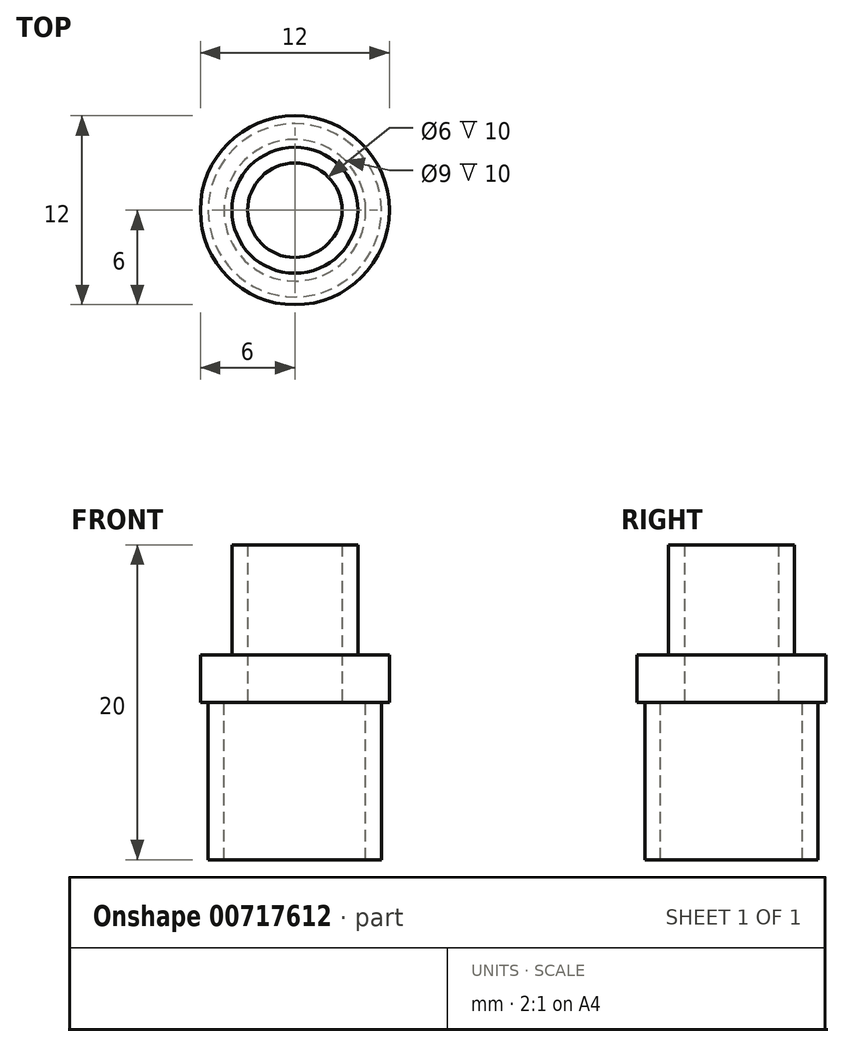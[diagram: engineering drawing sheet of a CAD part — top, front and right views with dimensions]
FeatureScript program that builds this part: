
annotation { "Feature Type Name" : "Feature", "Feature Type Description" : "" }
export const myFeature = defineFeature(function(context is Context, id is Id, definition is map)
    precondition{}
    {
        {
            var Q0;
            Q0=qCreatedBy(makeId("Top.planeOp"),FACE);
            var sketch = newSketch(context, id + "F0", { "sketchPlane" : qUnion([Q0])});
            skCircle(sketch, "E0", {"center": v(0, 0) * mm, "radius": 3 * mm});
            skCircle(sketch, "E1", {"center": v(0, 0) * mm, "radius": 4 * mm});
            skSolve(sketch);
        }
        {
            var Q0;
            Q0 = qSketchRegion(id + "F0", true);
            extrude(context, id + "F1", {"entities" : qUnion([Q0]), "depth" : 10 * mm, "offsetDistance" : 25 * mm});
        }
        {
            var Q0;
            Q0=qCreatedBy(makeId("Top.planeOp"),FACE);
            var sketch = newSketch(context, id + "F2", { "sketchPlane" : qUnion([Q0])});
            skCircle(sketch, "E2", {"center": v(0, 0) * mm, "radius": 3 * mm});
            skCircle(sketch, "E3", {"center": v(0, 0) * mm, "radius": 6 * mm});
            skSolve(sketch);
        }
        {
            var Q0;
            Q0 = qSketchRegion(id + "F2", true);
            extrude(context, id + "F3", {"entities" : qUnion([Q0]), "operationType" : NewBodyOperationType.ADD, "depth" : 3 * mm, "offsetDistance" : 25 * mm});
        }
        {
            var Q0;
            Q0=qCreatedBy(makeId("Top.planeOp"),FACE);
            var sketch = newSketch(context, id + "F4", { "sketchPlane" : qUnion([Q0])});
            skCircle(sketch, "E4", {"center": v(0, 0) * mm, "radius": 4.5 * mm});
            skCircle(sketch, "E5", {"center": v(0, 0) * mm, "radius": 5.5 * mm});
            skSolve(sketch);
        }
        {
            var Q0;
            Q0 = qSketchRegion(id + "F4", true);
            extrude(context, id + "F5", {"entities" : qUnion([Q0]), "operationType" : NewBodyOperationType.ADD, "oppositeDirection" : true, "depth" : 10 * mm, "offsetDistance" : 25 * mm});
        }
    });
